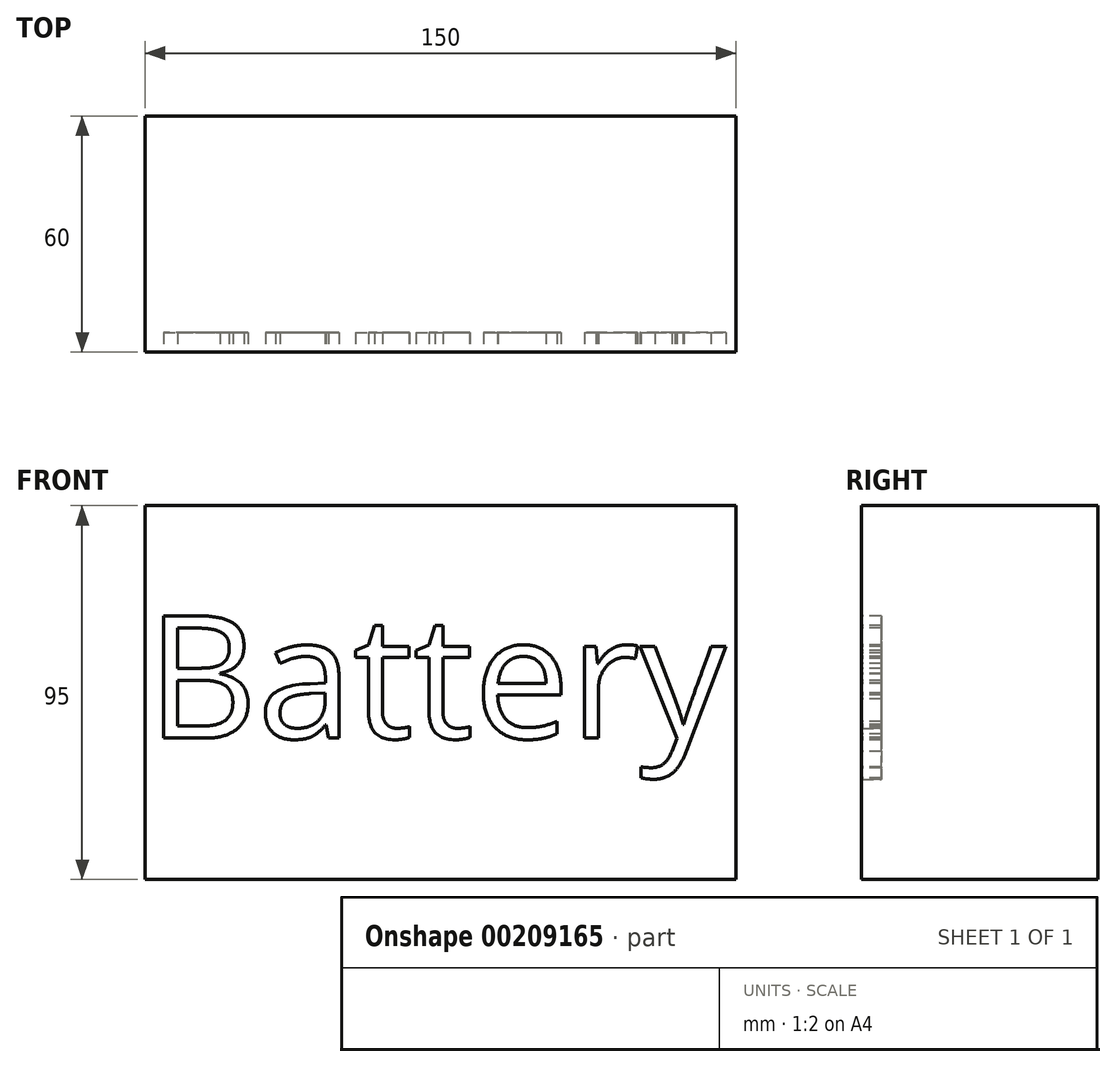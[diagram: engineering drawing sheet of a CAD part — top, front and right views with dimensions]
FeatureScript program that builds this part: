
annotation { "Feature Type Name" : "Feature", "Feature Type Description" : "" }
export const myFeature = defineFeature(function(context is Context, id is Id, definition is map)
    precondition{}
    {
        {
            var Q0;
            Q0=qCreatedBy(makeId("Front.planeOp"),FACE);
            var sketch = newSketch(context, id + "F0", { "sketchPlane" : qUnion([Q0])});
            skLineSegment(sketch, "E0.bottom", {"start": v(75, 47.5) * mm, "end": v(-75, 47.5) * mm});
            skLineSegment(sketch, "E0.top", {"start": v(75, -47.5) * mm, "end": v(-75, -47.5) * mm});
            skLineSegment(sketch, "E0.left", {"start": v(75, 47.5) * mm, "end": v(75, -47.5) * mm});
            skLineSegment(sketch, "E0.right", {"start": v(-75, 47.5) * mm, "end": v(-75, -47.5) * mm});
            skPoint(sketch, "E0.middle", {"position": v(0, 0) * mm});
            skSolve(sketch);
        }
        {
            var Q0;
            Q0 = qSketchRegion(id + "F0", true);
            extrude(context, id + "F1", {"entities" : qUnion([Q0]), "depth" : 60 * mm});
        }
        {
            var Q0;
            Q0=makeQuery(id+"F1.opExtrude","CAP_FACE",FACE,{"disambiguationData":[OSD([sQuery(id+"F0.wireOp",EDGE,"E0.bottom"),sQuery(id+"F0.wireOp",EDGE,"E0.top"),sQuery(id+"F0.wireOp",EDGE,"E0.left"),sQuery(id+"F0.wireOp",EDGE,"E0.right")])],"isStart":false});
            var sketch = newSketch(context, id + "F2", { "sketchPlane" : qUnion([Q0])});
            skText(sketch, "E1", { "text": "Battery", "fontName": "OpenSans-Regular.ttf"});
            const initialGuessF2  = {"E1": [-0.07468, -0.01157, 1, 0, 0.03133]};
            skSetInitialGuess(sketch, initialGuessF2);
            skSolve(sketch);
        }
        {
            var Q0;
            Q0 = qSketchRegion(id + "F2", true);
            extrude(context, id + "F3", {"entities" : qUnion([Q0]), "operationType" : NewBodyOperationType.REMOVE, "oppositeDirection" : true, "depth" : 5 * mm});
        }
    });
